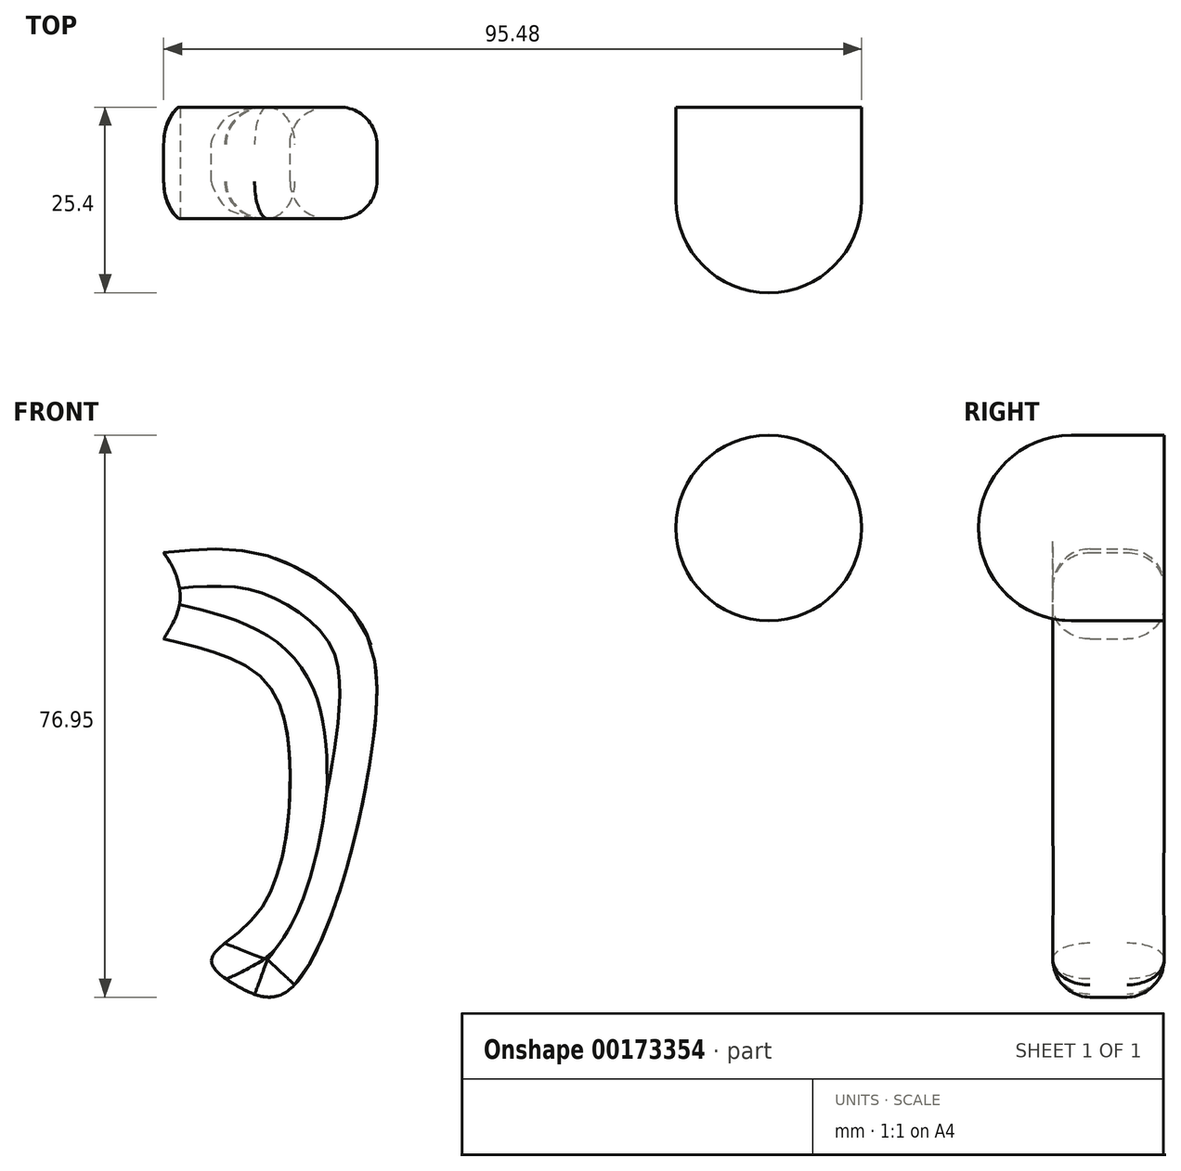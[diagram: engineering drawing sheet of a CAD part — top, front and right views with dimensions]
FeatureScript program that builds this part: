
annotation { "Feature Type Name" : "Feature", "Feature Type Description" : "" }
export const myFeature = defineFeature(function(context is Context, id is Id, definition is map)
    precondition{}
    {
        {
            var Q0;
            Q0=qCreatedBy(makeId("Front.planeOp"),FACE);
            var sketch = newSketch(context, id + "F0", { "sketchPlane" : qUnion([Q0])});
            skFitSpline(sketch, "E0", {"points": [v(-17.28, 30.82) * mm, v(-3.58, 30.5) * mm, v(8.56, 22.73) * mm, v(11.67, 7.78) * mm, v(0, -28.95) * mm, v(-7, -28.64) * mm, v(-10.74, -24.9) * mm, v(-4.51, -18.68) * mm, v(0, 0) * mm, v(-3.58, 13.39) * mm, v(-17.28, 19) * mm], "startDerivative": vector(138.83, 14.06) * mm, "endDerivative": vector(-156.47, 36.23) * mm});
            skFitSpline(sketch, "E1", {"points": [v(-17.28, 30.82) * mm, v(-15.75, 28.13) * mm, v(-15.1, 23.89) * mm, v(-17.28, 19) * mm], "startDerivative": vector(5.7, -8.65) * mm, "endDerivative": vector(-7.74, -12.88) * mm});
            skSolve(sketch);
        }
        {
            var Q0;
            Q0 = qSketchRegion(id + "F0", true);
            extrude(context, id + "F1", {"entities" : qUnion([Q0]), "depth" : 15.24 * mm});
        }
        {
            var Q0;
            Q0=makeQuery(id+"F1.opExtrude","CAP_EDGE",EDGE,{"disambiguationData":[OSD([sQuery(id+"F0.wireOp",EDGE,"E0")])],"isStart":true});
            fillet(context, id + "F2", {"entities" : qUnion([Q0]), "radius" : 5.08 * mm, "tangentPropagation" : true, "allowEdgeOverflow" : false});
        }
        {
            var Q0;
            Q0=makeQuery(id+"F1.opExtrude","CAP_EDGE",EDGE,{"disambiguationData":[OSD([sQuery(id+"F0.wireOp",EDGE,"E0")])],"isStart":false});
            fillet(context, id + "F3", {"entities" : qUnion([Q0]), "radius" : 5.08 * mm, "tangentPropagation" : true, "allowEdgeOverflow" : false});
        }
        {
            var Q0;
            Q0=qCreatedBy(makeId("Front.planeOp"),FACE);
            var sketch = newSketch(context, id + "F4", { "sketchPlane" : qUnion([Q0])});
            skCircle(sketch, "E2", {"center": v(65.5, 34.2) * mm, "radius": 12.7 * mm});
            skSolve(sketch);
        }
        {
            var Q0;
            Q0 = qSketchRegion(id + "F4", true);
            extrude(context, id + "F5", {"entities" : qUnion([Q0]), "depth" : 25.4 * mm});
        }
        {
            var Q0;
            Q0=makeQuery(id+"F5.opExtrude","CAP_FACE",FACE,{"disambiguationData":[OSD([sQuery(id+"F4.wireOp",EDGE,"E2")])],"isStart":false});
            fillet(context, id + "F6", {"entities" : qUnion([Q0]), "radius" : 12.7 * mm, "tangentPropagation" : true, "allowEdgeOverflow" : false});
        }
    });
